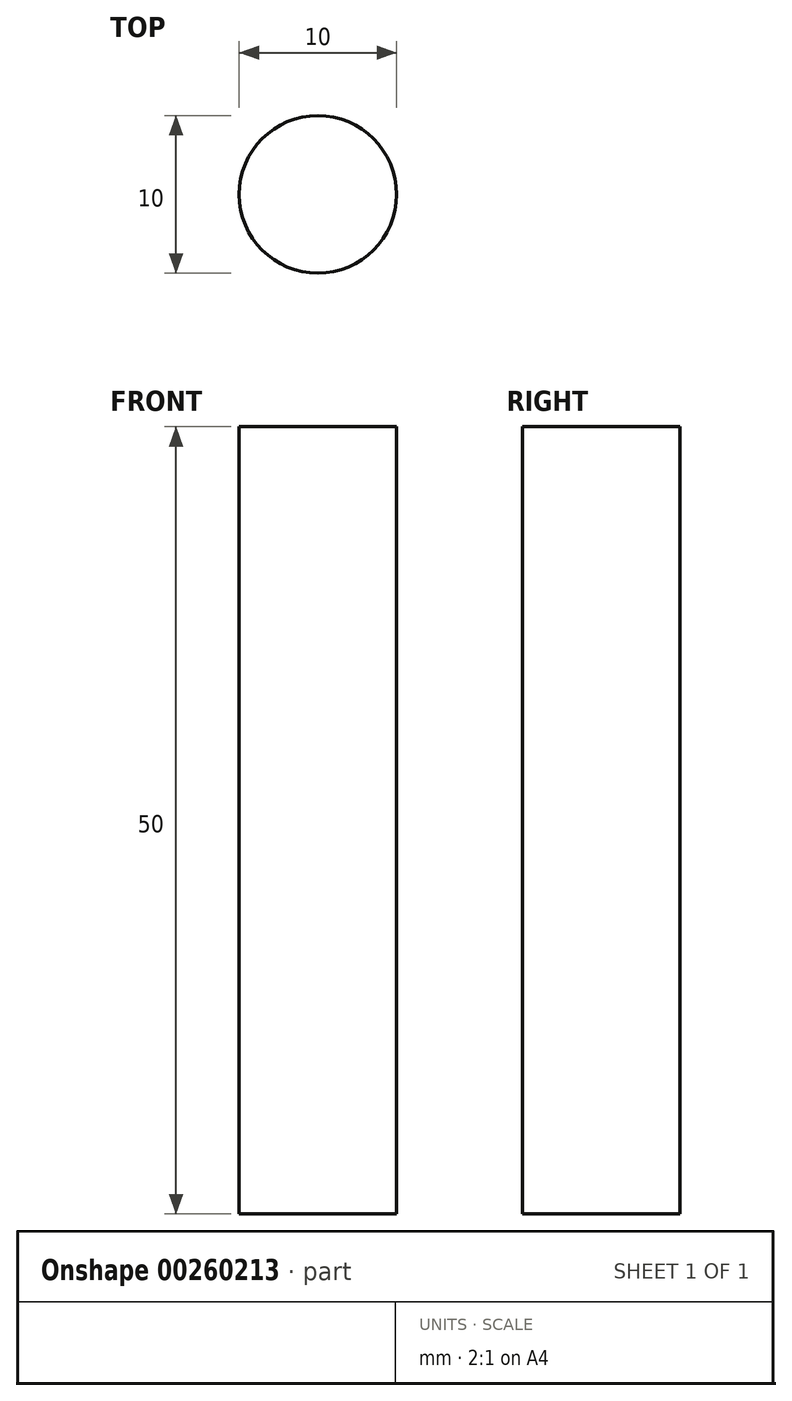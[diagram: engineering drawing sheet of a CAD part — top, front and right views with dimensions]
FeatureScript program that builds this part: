
annotation { "Feature Type Name" : "Feature", "Feature Type Description" : "" }
export const myFeature = defineFeature(function(context is Context, id is Id, definition is map)
    precondition{}
    {
        {
            var Q0;
            Q0=qCreatedBy(makeId("Top.planeOp"),FACE);
            var sketch = newSketch(context, id + "F0", { "sketchPlane" : qUnion([Q0])});
            skCircle(sketch, "E0", {"center": v(0, 0) * mm, "radius": 5 * mm});
            skSolve(sketch);
        }
        {
            var Q0;
            Q0=sQuery(id+"F0.wireOp",EDGE,"E0");
            extrude(context, id + "F1", {"bodyType" : ToolBodyType.SURFACE, "surfaceEntities" : qUnion([Q0]), "depth" : 50 * mm});
        }
    });
